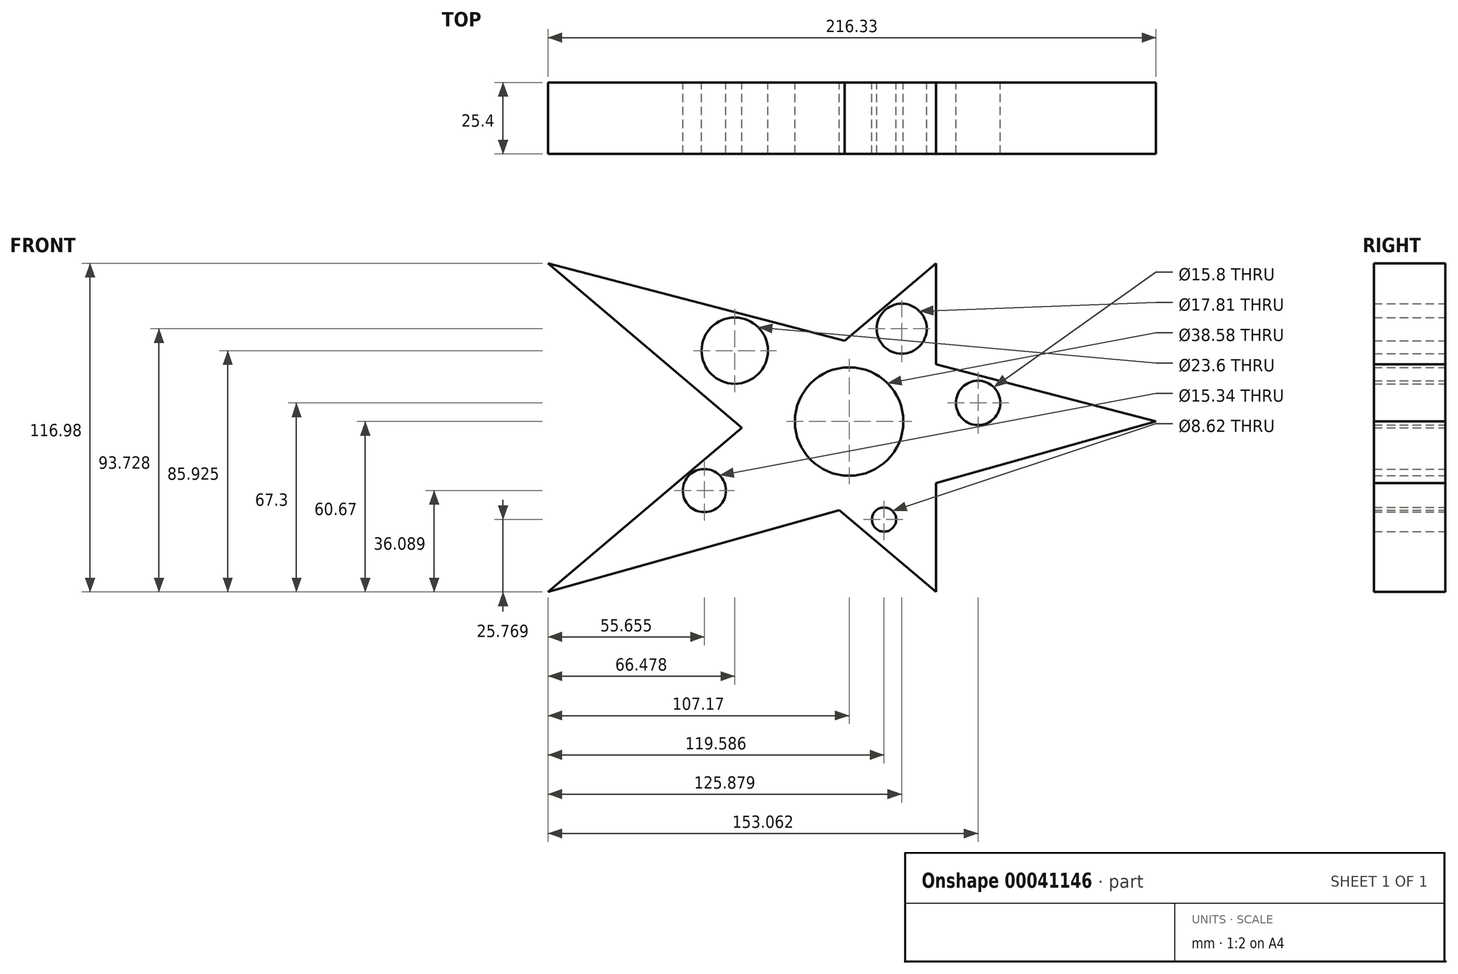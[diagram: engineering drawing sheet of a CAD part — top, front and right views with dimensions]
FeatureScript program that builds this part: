
annotation { "Feature Type Name" : "Feature", "Feature Type Description" : "" }
export const myFeature = defineFeature(function(context is Context, id is Id, definition is map)
    precondition{}
    {
        {
            var Q0;
            Q0=qCreatedBy(makeId("Front.planeOp"),FACE);
            var sketch = newSketch(context, id + "F0", { "sketchPlane" : qUnion([Q0])});
            skLineSegment(sketch, "E0", {"start": v(109.35, -60.67) * mm, "end": v(-107.17, -60.67) * mm});
            skLineSegment(sketch, "E1", {"start": v(-107.17, -60.67) * mm, "end": v(-107.17, 56.31) * mm});
            skLineSegment(sketch, "E2", {"start": v(-107.17, 56.31) * mm, "end": v(108.99, 56.31) * mm});
            skLineSegment(sketch, "E3", {"start": v(108.99, 56.31) * mm, "end": v(109.35, -60.67) * mm});
            skLineSegment(sketch, "E4", {"start": v(-107.17, -60.67) * mm, "end": v(109.16, 0) * mm});
            skLineSegment(sketch, "E5", {"start": v(109.16, 0) * mm, "end": v(-107.17, 56.31) * mm});
            skLineSegment(sketch, "E6", {"start": v(-107.17, 56.31) * mm, "end": v(30.88, -60.67) * mm});
            skLineSegment(sketch, "E7", {"start": v(30.88, -60.67) * mm, "end": v(30.88, 56.31) * mm});
            skLineSegment(sketch, "E8", {"start": v(30.88, 56.31) * mm, "end": v(-107.17, -60.67) * mm});
            skCircle(sketch, "E9", {"center": v(0, 0) * mm, "radius": 19.29 * mm});
            skCircle(sketch, "E10", {"center": v(-40.7, 25.26) * mm, "radius": 11.8 * mm});
            skCircle(sketch, "E11", {"center": v(18.7, 33.06) * mm, "radius": 8.9 * mm});
            skCircle(sketch, "E12", {"center": v(45.9, 6.63) * mm, "radius": 7.9 * mm});
            skCircle(sketch, "E13", {"center": v(12.42, -34.9) * mm, "radius": 4.3 * mm});
            skCircle(sketch, "E14", {"center": v(-51.52, -24.58) * mm, "radius": 7.67 * mm});
            skSolve(sketch);
        }
        {
            var Q0;
            Q0=makeQuery(id+"F0.imprint","IMPRINT",FACE,{"disambiguationData":[TD([[makeQuery(id+"F0.imprint","IMPRINT",EDGE,{"derivedFrom":sQuery(id+"F0.wireOp",EDGE,"E14")}),-1.0]])]});
            var Q1;
            Q1=makeQuery(id+"F0.imprint","IMPRINT",FACE,{"disambiguationData":[TD([[makeQuery(id+"F0.imprint","IMPRINT",EDGE,{"derivedFrom":sQuery(id+"F0.wireOp",EDGE,"E10")}),-1.0]])]});
            var Q2;
            Q2=makeQuery(id+"F0.imprint","IMPRINT",FACE,{"disambiguationData":[TD([[makeQuery(id+"F0.imprint","IMPRINT",EDGE,{"derivedFrom":sQuery(id+"F0.wireOp",EDGE,"E9")}),-1.0]])]});
            var Q3;
            Q3=makeQuery(id+"F0.imprint","IMPRINT",FACE,{"disambiguationData":[TD([[makeQuery(id+"F0.imprint","IMPRINT",EDGE,{"derivedFrom":sQuery(id+"F0.wireOp",EDGE,"E11")}),-1.0]])]});
            var Q4;
            Q4=makeQuery(id+"F0.imprint","IMPRINT",FACE,{"disambiguationData":[TD([[makeQuery(id+"F0.imprint","IMPRINT",EDGE,{"derivedFrom":sQuery(id+"F0.wireOp",EDGE,"E12")}),-1.0]])]});
            var Q5;
            Q5=makeQuery(id+"F0.imprint","IMPRINT",FACE,{"disambiguationData":[TD([[makeQuery(id+"F0.imprint","IMPRINT",EDGE,{"derivedFrom":sQuery(id+"F0.wireOp",EDGE,"E13")}),-1.0]])]});
            extrude(context, id + "F1", {"entities" : qUnion([Q0, Q1, Q2, Q3, Q4, Q5]), "depth" : 25.4 * mm});
        }
    });
